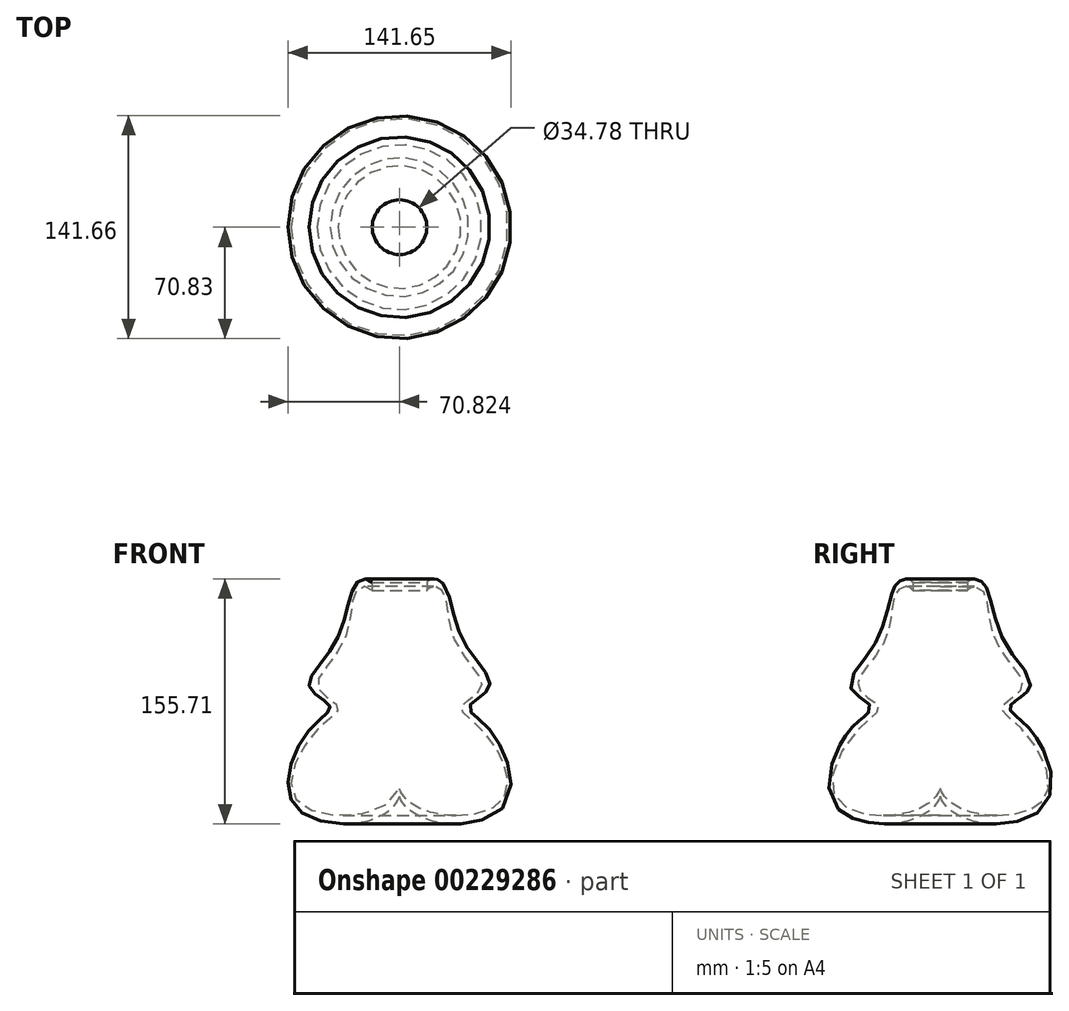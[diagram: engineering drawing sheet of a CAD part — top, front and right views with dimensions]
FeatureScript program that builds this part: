
annotation { "Feature Type Name" : "Feature", "Feature Type Description" : "" }
export const myFeature = defineFeature(function(context is Context, id is Id, definition is map)
    precondition{}
    {
        {
            var Q0;
            Q0=qCreatedBy(makeId("Front.planeOp"),FACE);
            var sketch = newSketch(context, id + "F0", { "sketchPlane" : qUnion([Q0])});
            skFitSpline(sketch, "E0", {"points": [v(-19.67, 78.64) * mm, v(-29.25, 78.64) * mm, v(-42.44, 41.85) * mm, v(-59.43, 12.44) * mm, v(-46.5, 0) * mm, v(-59.4, -14.65) * mm, v(-66.92, -65.29) * mm, v(-2.28, -57.2) * mm], "startDerivative": vector(-76.55, 132.54) * mm, "endDerivative": vector(115.38, 299.8) * mm});
            skLineSegment(sketch, "E1", {"start": v(-19.67, 78.64) * mm, "end": v(-19.67, 73.64) * mm});
            skFitSpline(sketch, "E2", {"points": [v(-19.67, 73.64) * mm, v(-29.25, 73.64) * mm, v(-37.44, 41.85) * mm, v(-54.43, 12.44) * mm, v(-41.5, 0) * mm, v(-54.4, -14.65) * mm, v(-66.92, -60.29) * mm, v(-2.28, -52.2) * mm], "startDerivative": vector(-74.98, 129.84) * mm, "endDerivative": vector(113.02, 293.67) * mm});
            skLineSegment(sketch, "E3", {"start": v(-2.28, -52.2) * mm, "end": v(-2.28, -57.2) * mm});
            skLineSegment(sketch, "E4", {"start": v(-2.28, -52.2) * mm, "end": v(-2.28, 78.64) * mm, "construction": true});
            skSolve(sketch);
        }
        {
            var Q0;
            Q0=makeQuery(id+"F0.imprint","IMPRINT",FACE,{"disambiguationData":[TD([[makeQuery(id+"F0.imprint","IMPRINT",EDGE,{"derivedFrom":sQuery(id+"F0.wireOp",EDGE,"E0")}),1.0]])]});
            var Q1;
            Q1=sQuery(id+"F0.wireOp",EDGE,"E4");
            revolve(context, id + "F1", {"entities" : qUnion([Q0]), "axis" : qUnion([Q1]), "revolveType" : RevolveType.FULL});
        }
    });
